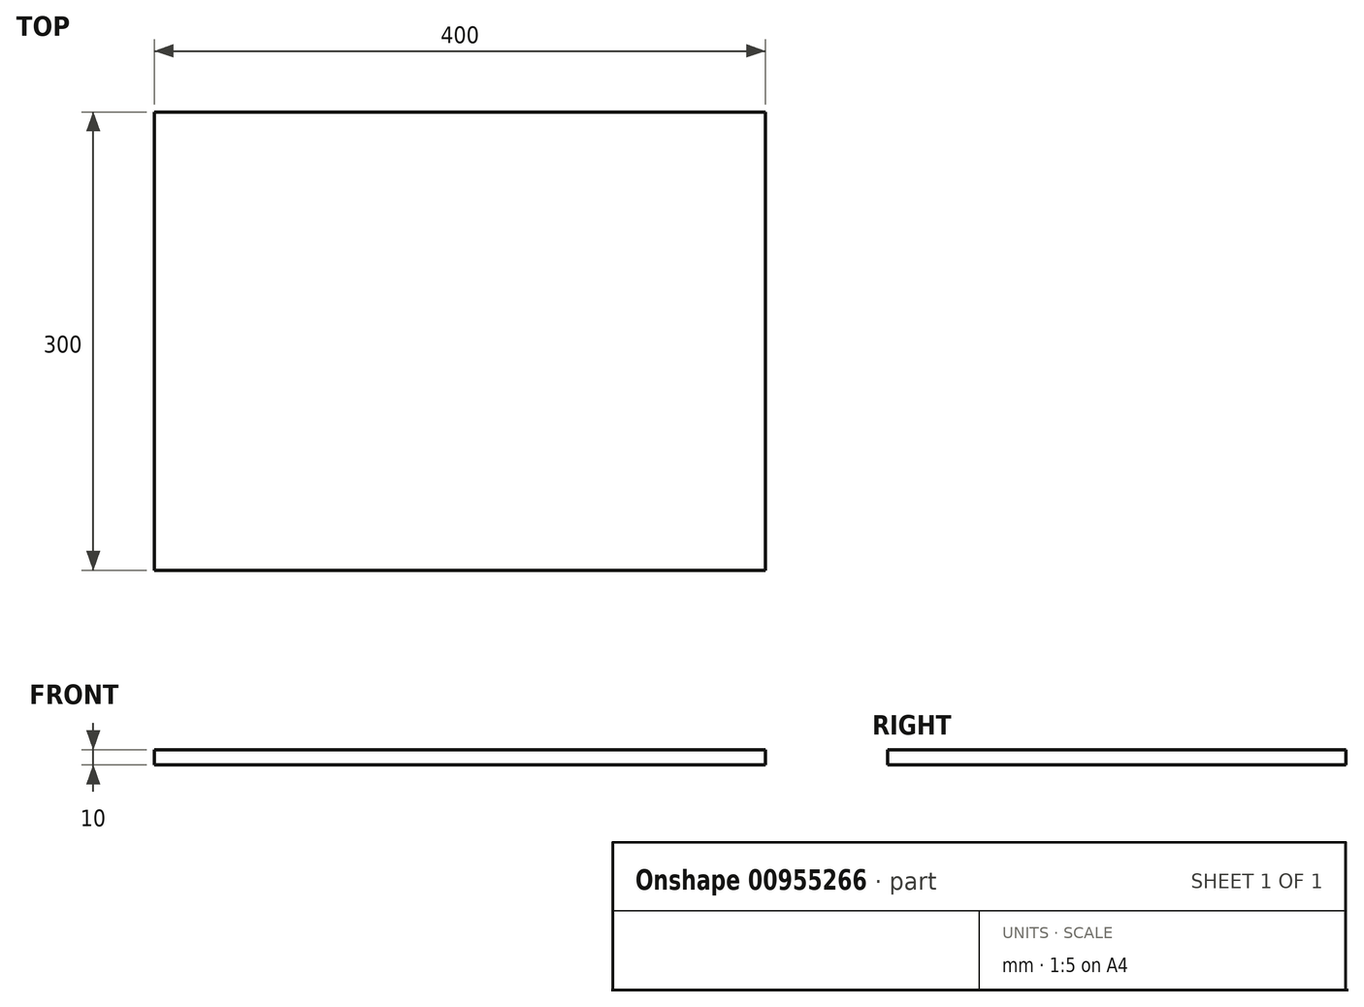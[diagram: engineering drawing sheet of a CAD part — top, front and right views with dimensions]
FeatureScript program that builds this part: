
annotation { "Feature Type Name" : "Feature", "Feature Type Description" : "" }
export const myFeature = defineFeature(function(context is Context, id is Id, definition is map)
    precondition{}
    {
        {
            var Q0;
            Q0=qCreatedBy(makeId("Top.planeOp"),FACE);
            var sketch = newSketch(context, id + "F0", { "sketchPlane" : qUnion([Q0])});
            skLineSegment(sketch, "E0.bottom", {"start": v(200, -150) * mm, "end": v(-200, -150) * mm});
            skLineSegment(sketch, "E0.top", {"start": v(200, 150) * mm, "end": v(-200, 150) * mm});
            skLineSegment(sketch, "E0.left", {"start": v(200, -150) * mm, "end": v(200, 150) * mm});
            skLineSegment(sketch, "E0.right", {"start": v(-200, -150) * mm, "end": v(-200, 150) * mm});
            skPoint(sketch, "E0.middle", {"position": v(0, 0) * mm});
            skSolve(sketch);
        }
        {
            var Q0;
            Q0=makeQuery(id+"F0.imprint","IMPRINT",FACE,{"disambiguationData":[TD([[makeQuery(id+"F0.imprint","IMPRINT",EDGE,{"derivedFrom":sQuery(id+"F0.wireOp",EDGE,"E0.bottom")}),-1.0]])]});
            extrude(context, id + "F1", {"entities" : qUnion([Q0]), "depth" : 10 * mm, "offsetDistance" : 25 * mm});
        }
    });
